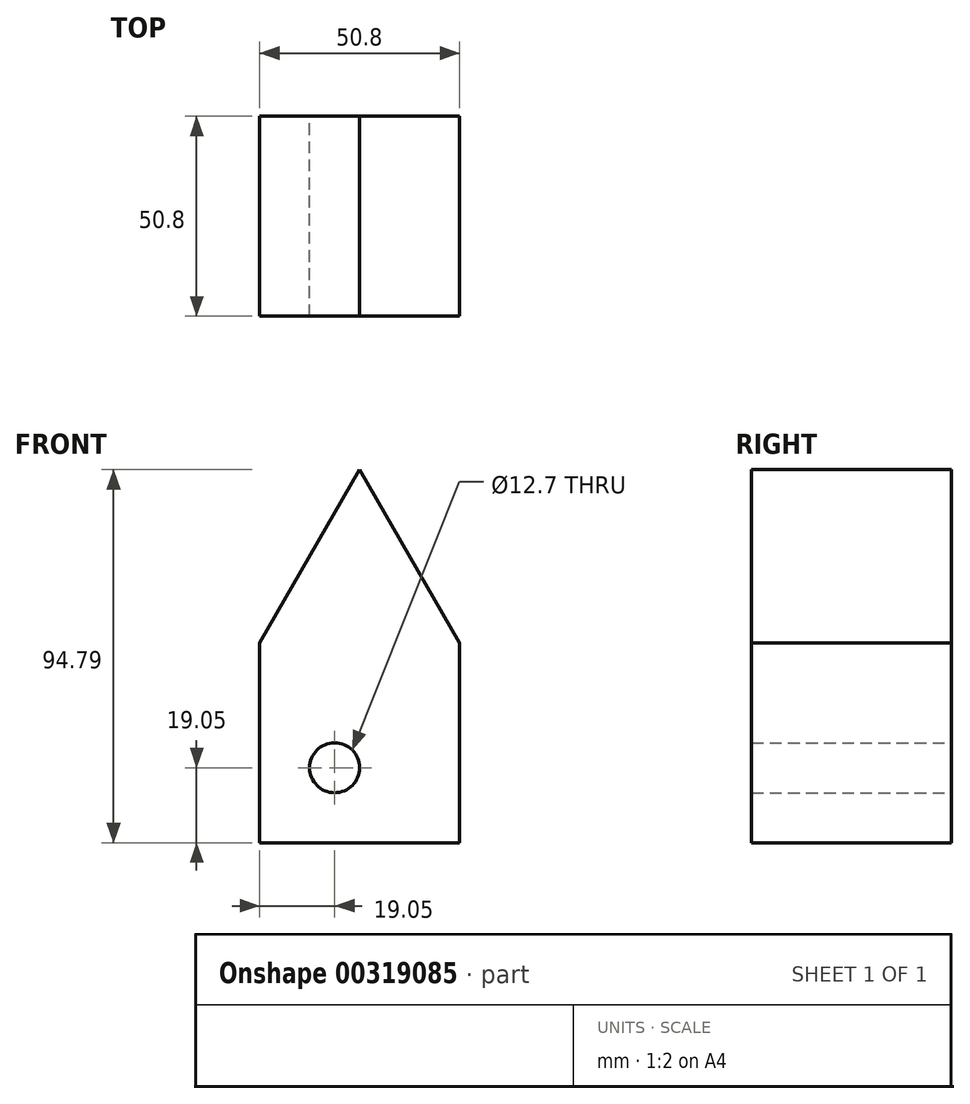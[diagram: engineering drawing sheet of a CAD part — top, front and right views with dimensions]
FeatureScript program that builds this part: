
annotation { "Feature Type Name" : "Feature", "Feature Type Description" : "" }
export const myFeature = defineFeature(function(context is Context, id is Id, definition is map)
    precondition{}
    {
        {
            var Q0;
            Q0=qCreatedBy(makeId("Front.planeOp"),FACE);
            var sketch = newSketch(context, id + "F0", { "sketchPlane" : qUnion([Q0])});
            skLineSegment(sketch, "E0.top", {"start": v(-25.4, -25.4) * mm, "end": v(25.4, -25.4) * mm});
            skLineSegment(sketch, "E0.left", {"start": v(-25.4, 25.4) * mm, "end": v(-25.4, -25.4) * mm});
            skLineSegment(sketch, "E0.right", {"start": v(25.4, 25.4) * mm, "end": v(25.4, -25.4) * mm});
            skPoint(sketch, "E0.middle", {"position": v(0, 0) * mm});
            skLineSegment(sketch, "E1", {"start": v(-25.4, 25.4) * mm, "end": v(0, 69.4) * mm});
            skLineSegment(sketch, "E2", {"start": v(0, 69.4) * mm, "end": v(25.4, 25.4) * mm});
            skCircle(sketch, "E3", {"center": v(-6.35, -6.35) * mm, "radius": 6.35 * mm});
            skSolve(sketch);
        }
        {
            var Q0;
            Q0=makeQuery(id+"F0.imprint","IMPRINT",FACE,{"disambiguationData":[TD([[makeQuery(id+"F0.imprint","IMPRINT",EDGE,{"derivedFrom":sQuery(id+"F0.wireOp",EDGE,"E0.top")}),1.0]])]});
            extrude(context, id + "F1", {"entities" : qUnion([Q0]), "depth" : 50.8 * mm});
        }
    });
